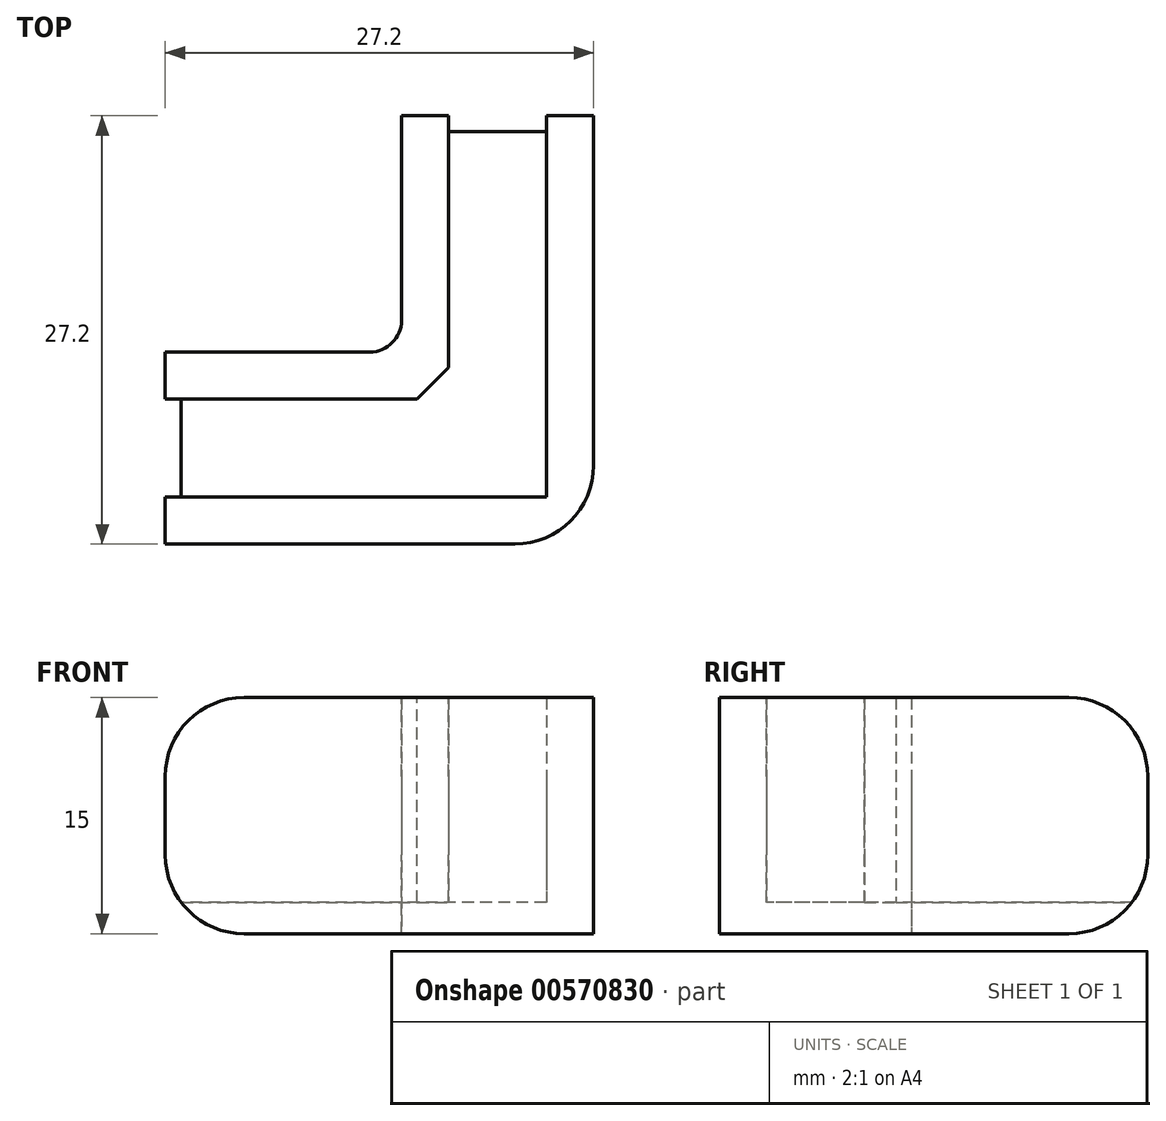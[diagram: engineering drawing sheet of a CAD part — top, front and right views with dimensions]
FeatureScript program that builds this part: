
annotation { "Feature Type Name" : "Feature", "Feature Type Description" : "" }
export const myFeature = defineFeature(function(context is Context, id is Id, definition is map)
    precondition{}
    {
        {
            var Q0;
            Q0=qCreatedBy(makeId("Top.planeOp"),FACE);
            var sketch = newSketch(context, id + "F0", { "sketchPlane" : qUnion([Q0])});
            skLineSegment(sketch, "E0", {"start": v(0.92, 6.2) * mm, "end": v(0.92, 24.2) * mm});
            skLineSegment(sketch, "E1", {"start": v(-5.28, 24.2) * mm, "end": v(-5.28, 6.2) * mm});
            skLineSegment(sketch, "E2", {"start": v(-5.28, 6.2) * mm, "end": v(-23.28, 6.2) * mm});
            skLineSegment(sketch, "E3", {"start": v(-23.28, 0) * mm, "end": v(0, 0) * mm});
            skLineSegment(sketch, "E4.0", {"start": v(3.92, 24.2) * mm, "end": v(-8.28, 24.2) * mm});
            skLineSegment(sketch, "E4.2", {"start": v(-8.28, 24.2) * mm, "end": v(-8.28, 9.2) * mm});
            skLineSegment(sketch, "E4.5", {"start": v(-8.28, 9.2) * mm, "end": v(-23.28, 9.2) * mm});
            skLineSegment(sketch, "E4.6", {"start": v(-23.28, 9.2) * mm, "end": v(-23.28, -3) * mm});
            skLineSegment(sketch, "E4.7", {"start": v(-23.28, -3) * mm, "end": v(0, -3) * mm});
            skLineSegment(sketch, "E5", {"start": v(3.92, 24.2) * mm, "end": v(3.92, -3) * mm});
            skLineSegment(sketch, "E6", {"start": v(0, -3) * mm, "end": v(3.92, -3) * mm});
            skLineSegment(sketch, "E7", {"start": v(0, 0) * mm, "end": v(0.92, 0) * mm});
            skLineSegment(sketch, "E8", {"start": v(0.92, 0) * mm, "end": v(0.92, 6.2) * mm});
            skPoint(sketch, "E9", {"position": v(-2.18, 24.2) * mm});
            skSolve(sketch);
        }
        {
            var Q0;
            Q0=qSketchRegion(id+"F0",true);
            extrude(context, id + "F1", {"entities" : qUnion([Q0]), "depth" : 2 * mm, "offsetDistance" : 25 * mm});
        }
        {
            var Q0;
            {var subQ3=sQuery(id+"F0.wireOp",EDGE,"E1");Q0=makeQuery(id+"F0.imprint","IMPRINT",FACE,{"disambiguationData":[TD([[makeQuery(id+"F0.imprint","IMPRINT",EDGE,{"derivedFrom":subQ3}),-1.0]])]});}
            var Q1;
            {var subQ3=sQuery(id+"F0.wireOp",EDGE,"E0");Q1=makeQuery(id+"F0.imprint","IMPRINT",FACE,{"disambiguationData":[TD([[makeQuery(id+"F0.imprint","IMPRINT",EDGE,{"derivedFrom":subQ3}),-1.0]])]});}
            extrude(context, id + "F2", {"entities" : qUnion([Q0, Q1]), "operationType" : NewBodyOperationType.ADD, "depth" : 15 * mm, "offsetDistance" : 25 * mm});
        }
        {
            var Q0;
            {var subQ0=sQuery(id+"F0.wireOp",EDGE,"E4.4");Q0=makeQuery(id+"F2.opExtrude","CAP_EDGE",EDGE,{"disambiguationData":[OSD([subQ0]),TDD([makeQuery(id+"F0.imprint","IMPRINT",EDGE,{"disambiguationData":[TD([[makeQuery(id+"F0.imprint","INTERSECT",VERTEX,{"derivedFrom":[sQuery(id+"F0.wireOp",EDGE,"4AKFVKuP-VGzW-Z0gR-biP7-avwRZvC0l9sY"),subQ0]}),1.0]])],"derivedFrom":subQ0})])],"isStart":false});}
            var Q1;
            {var subQ0=sQuery(id+"F0.wireOp",EDGE,"E4.4");Q1=makeQuery(id+"F2.opExtrude","CAP_EDGE",EDGE,{"disambiguationData":[OSD([subQ0]),TDD([makeQuery(id+"F0.imprint","IMPRINT",EDGE,{"disambiguationData":[TD([[makeQuery(id+"F0.imprint","INTERSECT",VERTEX,{"derivedFrom":[sQuery(id+"F0.wireOp",EDGE,"wGMG52vS-Bb6S-6M2K-uLHt-X8AWWQIAXK16"),subQ0]}),-1.0]])],"derivedFrom":subQ0})])],"isStart":false});}
            var Q2;
            {var subQ0=sQuery(id+"F0.wireOp",EDGE,"E4.6");Q2=makeQuery(id+"F2.opExtrude","CAP_EDGE",EDGE,{"disambiguationData":[OSD([subQ0]),TDD([makeQuery(id+"F0.imprint","IMPRINT",EDGE,{"disambiguationData":[TD([[makeQuery(id+"F0.imprint","INTERSECT",VERTEX,{"derivedFrom":[sQuery(id+"F0.wireOp",EDGE,"E3"),subQ0]}),-1.0]])],"derivedFrom":subQ0})])],"isStart":false});}
            var Q3;
            {var subQ0=sQuery(id+"F0.wireOp",EDGE,"E4.6");Q3=makeQuery(id+"F2.opExtrude","CAP_EDGE",EDGE,{"disambiguationData":[OSD([subQ0]),TDD([makeQuery(id+"F0.imprint","IMPRINT",EDGE,{"disambiguationData":[TD([[makeQuery(id+"F0.imprint","INTERSECT",VERTEX,{"derivedFrom":[sQuery(id+"F0.wireOp",EDGE,"E2"),subQ0]}),1.0]])],"derivedFrom":subQ0})])],"isStart":false});}
            var Q4;
            {var subQ0=sQuery(id+"F0.wireOp",EDGE,"E4.0");Q4=makeQuery(id+"F2.opExtrude","CAP_EDGE",EDGE,{"disambiguationData":[OSD([subQ0]),TDD([makeQuery(id+"F0.imprint","IMPRINT",EDGE,{"disambiguationData":[TD([[makeQuery(id+"F0.imprint","INTERSECT",VERTEX,{"derivedFrom":[sQuery(id+"F0.wireOp",EDGE,"E1"),subQ0]}),-1.0]])],"derivedFrom":subQ0})])],"isStart":false});}
            var Q5;
            {var subQ0=sQuery(id+"F0.wireOp",EDGE,"E4.0");Q5=makeQuery(id+"F2.opExtrude","CAP_EDGE",EDGE,{"disambiguationData":[OSD([subQ0]),TDD([makeQuery(id+"F0.imprint","IMPRINT",EDGE,{"disambiguationData":[TD([[makeQuery(id+"F0.imprint","INTERSECT",VERTEX,{"derivedFrom":[sQuery(id+"F0.wireOp",EDGE,"E0"),subQ0]}),1.0]])],"derivedFrom":subQ0})])],"isStart":false});}
            var Q6;
            Q6=makeQuery(id+"F1.opExtrude","CAP_EDGE",EDGE,{"disambiguationData":[OSD([sQuery(id+"F0.wireOp",EDGE,"E4.6")])],"isStart":true});
            var Q7;
            Q7=makeQuery(id+"F1.opExtrude","CAP_EDGE",EDGE,{"disambiguationData":[OSD([sQuery(id+"F0.wireOp",EDGE,"E4.4")])],"isStart":true});
            var Q8;
            Q8=makeQuery(id+"F1.opExtrude","CAP_EDGE",EDGE,{"disambiguationData":[OSD([sQuery(id+"F0.wireOp",EDGE,"E4.0")])],"isStart":true});
            var Q9;
            {var subQ0=sQuery(id+"F0.wireOp",EDGE,"E6");var subQ1=sQuery(id+"F0.wireOp",EDGE,"E5");Q9=makeQuery(id+"F2.boolean.opBoolean","MERGE",EDGE,{"derivedFrom":[makeQuery(id+"F1.opExtrude","SWEPT_EDGE",EDGE,{"disambiguationData":[OSD([subQ1,subQ0])]}),makeQuery(id+"F2.opExtrude","SWEPT_EDGE",EDGE,{"disambiguationData":[OSD([subQ1,subQ0])]})]});}
            fillet(context, id + "F3", {"entities" : qUnion([Q0, Q1, Q2, Q3, Q4, Q5, Q6, Q7, Q8, Q9]), "radius" : 5 * mm, "tangentPropagation" : true, "allowEdgeOverflow" : false});
        }
        {
            var Q0;
            {var subQ0=sQuery(id+"F0.wireOp",EDGE,"E4.5");var subQ1=sQuery(id+"F0.wireOp",EDGE,"E4.2");Q0=makeQuery(id+"F2.boolean.opBoolean","MERGE",EDGE,{"derivedFrom":[makeQuery(id+"F1.opExtrude","SWEPT_EDGE",EDGE,{"disambiguationData":[OSD([subQ1,subQ0])]}),makeQuery(id+"F2.opExtrude","SWEPT_EDGE",EDGE,{"disambiguationData":[OSD([subQ1,subQ0])]})]});}
            fillet(context, id + "F4", {"entities" : qUnion([Q0]), "radius" : 2 * mm, "tangentPropagation" : true, "allowEdgeOverflow" : false});
        }
        {
            var Q0;
            Q0=makeQuery(id+"F2.opExtrude","SWEPT_EDGE",EDGE,{"disambiguationData":[OSD([sQuery(id+"F0.wireOp",EDGE,"E1"),sQuery(id+"F0.wireOp",EDGE,"E2")])]});
            chamfer(context, id + "F5", {"entities" : qUnion([Q0]), "width" : 2 * mm, "tangentPropagation" : true});
        }
    });
